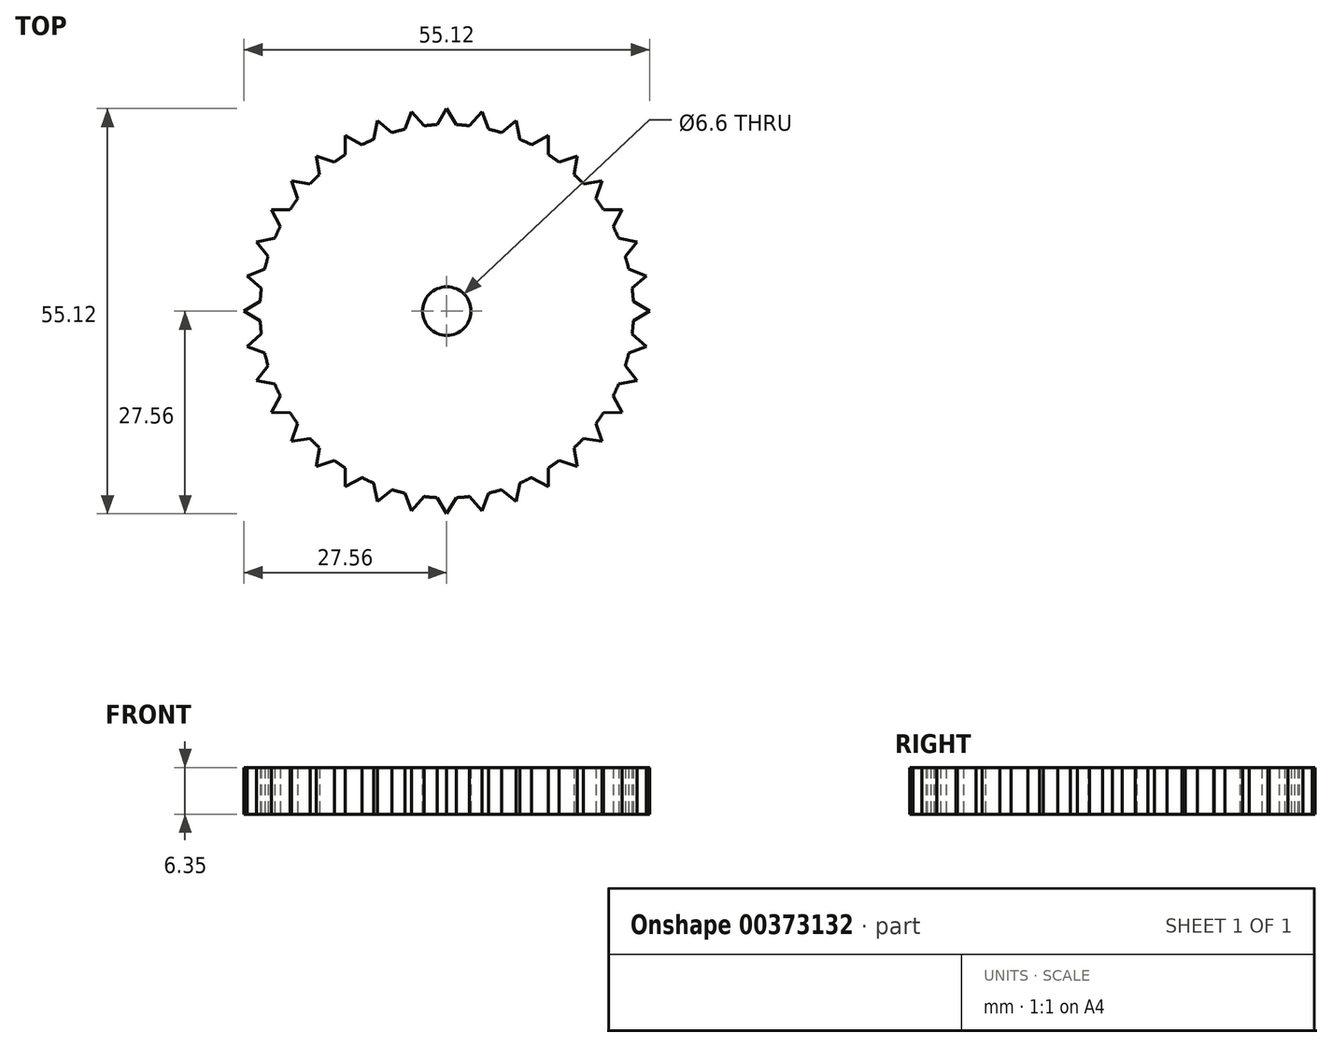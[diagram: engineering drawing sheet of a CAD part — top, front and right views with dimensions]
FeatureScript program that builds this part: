
annotation { "Feature Type Name" : "Feature", "Feature Type Description" : "" }
export const myFeature = defineFeature(function(context is Context, id is Id, definition is map)
    precondition{}
    {
        {
            var Q0;
            Q0=qCreatedBy(makeId("Top.planeOp"),FACE);
            var sketch = newSketch(context, id + "F0", { "sketchPlane" : qUnion([Q0])});
            skCircle(sketch, "E0", {"center": v(0, 0) * mm, "radius": 25.4 * mm});
            skCircle(sketch, "E1", {"center": v(0, 0) * mm, "radius": 3.3 * mm});
            skLineSegment(sketch, "E2", {"start": v(0, 25.4) * mm, "end": v(0, 27.56) * mm});
            skLineSegment(sketch, "E3", {"start": v(0, 27.56) * mm, "end": v(-1.32, 25.37) * mm});
            skLineSegment(sketch, "E4", {"start": v(0, 27.56) * mm, "end": v(1.32, 25.37) * mm});
            skLineSegment(sketch, "E5.1.0", {"start": v(-4.79, 27.15) * mm, "end": v(-5.7, 24.75) * mm});
            skLineSegment(sketch, "E5.1.1", {"start": v(-4.79, 27.15) * mm, "end": v(-3.1, 25.2) * mm});
            skLineSegment(sketch, "E5.2.0", {"start": v(-9.43, 25.9) * mm, "end": v(-9.92, 23.38) * mm});
            skLineSegment(sketch, "E5.2.1", {"start": v(-9.43, 25.9) * mm, "end": v(-7.43, 24.29) * mm});
            skLineSegment(sketch, "E5.3.0", {"start": v(-13.78, 23.87) * mm, "end": v(-13.83, 21.3) * mm});
            skLineSegment(sketch, "E5.3.1", {"start": v(-13.78, 23.87) * mm, "end": v(-11.54, 22.63) * mm});
            skLineSegment(sketch, "E5.4.0", {"start": v(-17.72, 21.12) * mm, "end": v(-17.32, 18.58) * mm});
            skLineSegment(sketch, "E5.4.1", {"start": v(-17.72, 21.12) * mm, "end": v(-15.3, 20.28) * mm});
            skLineSegment(sketch, "E5.5.0", {"start": v(-21.12, 17.72) * mm, "end": v(-20.28, 15.3) * mm});
            skLineSegment(sketch, "E5.5.1", {"start": v(-21.12, 17.72) * mm, "end": v(-18.58, 17.32) * mm});
            skLineSegment(sketch, "E5.6.0", {"start": v(-23.87, 13.78) * mm, "end": v(-22.63, 11.54) * mm});
            skLineSegment(sketch, "E5.6.1", {"start": v(-23.87, 13.78) * mm, "end": v(-21.3, 13.83) * mm});
            skLineSegment(sketch, "E5.7.0", {"start": v(-25.9, 9.43) * mm, "end": v(-24.29, 7.43) * mm});
            skLineSegment(sketch, "E5.7.1", {"start": v(-25.9, 9.43) * mm, "end": v(-23.38, 9.92) * mm});
            skLineSegment(sketch, "E5.8.0", {"start": v(-27.15, 4.79) * mm, "end": v(-25.2, 3.1) * mm});
            skLineSegment(sketch, "E5.8.1", {"start": v(-27.15, 4.79) * mm, "end": v(-24.75, 5.7) * mm});
            skLineSegment(sketch, "E5.9.0", {"start": v(-27.56, 0) * mm, "end": v(-25.37, -1.32) * mm});
            skLineSegment(sketch, "E5.9.1", {"start": v(-27.56, 0) * mm, "end": v(-25.37, 1.32) * mm});
            skLineSegment(sketch, "E5.10.0", {"start": v(-27.15, -4.79) * mm, "end": v(-24.75, -5.7) * mm});
            skLineSegment(sketch, "E5.10.1", {"start": v(-27.15, -4.79) * mm, "end": v(-25.2, -3.1) * mm});
            skLineSegment(sketch, "E5.11.0", {"start": v(-25.9, -9.43) * mm, "end": v(-23.38, -9.92) * mm});
            skLineSegment(sketch, "E5.11.1", {"start": v(-25.9, -9.43) * mm, "end": v(-24.29, -7.43) * mm});
            skLineSegment(sketch, "E5.12.0", {"start": v(-23.87, -13.78) * mm, "end": v(-21.3, -13.83) * mm});
            skLineSegment(sketch, "E5.12.1", {"start": v(-23.87, -13.78) * mm, "end": v(-22.63, -11.54) * mm});
            skLineSegment(sketch, "E5.13.0", {"start": v(-21.12, -17.72) * mm, "end": v(-18.58, -17.32) * mm});
            skLineSegment(sketch, "E5.13.1", {"start": v(-21.12, -17.72) * mm, "end": v(-20.28, -15.3) * mm});
            skLineSegment(sketch, "E5.14.0", {"start": v(-17.72, -21.12) * mm, "end": v(-15.3, -20.28) * mm});
            skLineSegment(sketch, "E5.14.1", {"start": v(-17.72, -21.12) * mm, "end": v(-17.32, -18.58) * mm});
            skLineSegment(sketch, "E5.15.0", {"start": v(-13.78, -23.87) * mm, "end": v(-11.54, -22.63) * mm});
            skLineSegment(sketch, "E5.15.1", {"start": v(-13.78, -23.87) * mm, "end": v(-13.83, -21.3) * mm});
            skLineSegment(sketch, "E5.16.0", {"start": v(-9.43, -25.9) * mm, "end": v(-7.43, -24.29) * mm});
            skLineSegment(sketch, "E5.16.1", {"start": v(-9.43, -25.9) * mm, "end": v(-9.92, -23.38) * mm});
            skLineSegment(sketch, "E5.17.0", {"start": v(-4.79, -27.15) * mm, "end": v(-3.1, -25.2) * mm});
            skLineSegment(sketch, "E5.17.1", {"start": v(-4.79, -27.15) * mm, "end": v(-5.7, -24.75) * mm});
            skLineSegment(sketch, "E5.18.0", {"start": v(0, -27.56) * mm, "end": v(1.32, -25.37) * mm});
            skLineSegment(sketch, "E5.18.1", {"start": v(0, -27.56) * mm, "end": v(-1.32, -25.37) * mm});
            skLineSegment(sketch, "E5.19.0", {"start": v(4.79, -27.15) * mm, "end": v(5.7, -24.75) * mm});
            skLineSegment(sketch, "E5.19.1", {"start": v(4.79, -27.15) * mm, "end": v(3.1, -25.2) * mm});
            skLineSegment(sketch, "E5.20.0", {"start": v(9.43, -25.9) * mm, "end": v(9.92, -23.38) * mm});
            skLineSegment(sketch, "E5.20.1", {"start": v(9.43, -25.9) * mm, "end": v(7.43, -24.29) * mm});
            skLineSegment(sketch, "E5.21.0", {"start": v(13.78, -23.87) * mm, "end": v(13.83, -21.3) * mm});
            skLineSegment(sketch, "E5.21.1", {"start": v(13.78, -23.87) * mm, "end": v(11.54, -22.63) * mm});
            skLineSegment(sketch, "E5.22.0", {"start": v(17.72, -21.12) * mm, "end": v(17.32, -18.58) * mm});
            skLineSegment(sketch, "E5.22.1", {"start": v(17.72, -21.12) * mm, "end": v(15.3, -20.28) * mm});
            skLineSegment(sketch, "E5.23.0", {"start": v(21.12, -17.72) * mm, "end": v(20.28, -15.3) * mm});
            skLineSegment(sketch, "E5.23.1", {"start": v(21.12, -17.72) * mm, "end": v(18.58, -17.32) * mm});
            skLineSegment(sketch, "E5.24.0", {"start": v(23.87, -13.78) * mm, "end": v(22.63, -11.54) * mm});
            skLineSegment(sketch, "E5.24.1", {"start": v(23.87, -13.78) * mm, "end": v(21.3, -13.83) * mm});
            skLineSegment(sketch, "E5.25.0", {"start": v(25.9, -9.43) * mm, "end": v(24.29, -7.43) * mm});
            skLineSegment(sketch, "E5.25.1", {"start": v(25.9, -9.43) * mm, "end": v(23.38, -9.92) * mm});
            skLineSegment(sketch, "E5.26.0", {"start": v(27.15, -4.79) * mm, "end": v(25.2, -3.1) * mm});
            skLineSegment(sketch, "E5.26.1", {"start": v(27.15, -4.79) * mm, "end": v(24.75, -5.7) * mm});
            skLineSegment(sketch, "E5.27.0", {"start": v(27.56, 0) * mm, "end": v(25.37, 1.32) * mm});
            skLineSegment(sketch, "E5.27.1", {"start": v(27.56, 0) * mm, "end": v(25.37, -1.32) * mm});
            skLineSegment(sketch, "E5.28.0", {"start": v(27.15, 4.79) * mm, "end": v(24.75, 5.7) * mm});
            skLineSegment(sketch, "E5.28.1", {"start": v(27.15, 4.79) * mm, "end": v(25.2, 3.1) * mm});
            skLineSegment(sketch, "E5.29.0", {"start": v(25.9, 9.43) * mm, "end": v(23.38, 9.92) * mm});
            skLineSegment(sketch, "E5.29.1", {"start": v(25.9, 9.43) * mm, "end": v(24.29, 7.43) * mm});
            skLineSegment(sketch, "E5.30.0", {"start": v(23.87, 13.78) * mm, "end": v(21.3, 13.83) * mm});
            skLineSegment(sketch, "E5.30.1", {"start": v(23.87, 13.78) * mm, "end": v(22.63, 11.54) * mm});
            skLineSegment(sketch, "E5.31.0", {"start": v(21.12, 17.72) * mm, "end": v(18.58, 17.32) * mm});
            skLineSegment(sketch, "E5.31.1", {"start": v(21.12, 17.72) * mm, "end": v(20.28, 15.3) * mm});
            skLineSegment(sketch, "E5.32.0", {"start": v(17.72, 21.12) * mm, "end": v(15.3, 20.28) * mm});
            skLineSegment(sketch, "E5.32.1", {"start": v(17.72, 21.12) * mm, "end": v(17.32, 18.58) * mm});
            skLineSegment(sketch, "E5.33.0", {"start": v(13.78, 23.87) * mm, "end": v(11.54, 22.63) * mm});
            skLineSegment(sketch, "E5.33.1", {"start": v(13.78, 23.87) * mm, "end": v(13.83, 21.3) * mm});
            skLineSegment(sketch, "E5.34.0", {"start": v(9.43, 25.9) * mm, "end": v(7.43, 24.29) * mm});
            skLineSegment(sketch, "E5.34.1", {"start": v(9.43, 25.9) * mm, "end": v(9.92, 23.38) * mm});
            skLineSegment(sketch, "E5.35.0", {"start": v(4.79, 27.15) * mm, "end": v(3.1, 25.2) * mm});
            skLineSegment(sketch, "E5.35.1", {"start": v(4.79, 27.15) * mm, "end": v(5.7, 24.75) * mm});
            skSolve(sketch);
        }
        {
            var Q0;
            Q0 = qSketchRegion(id + "F0", true);
            extrude(context, id + "F1", {"entities" : qUnion([Q0]), "depth" : 6.35 * mm});
        }
    });
